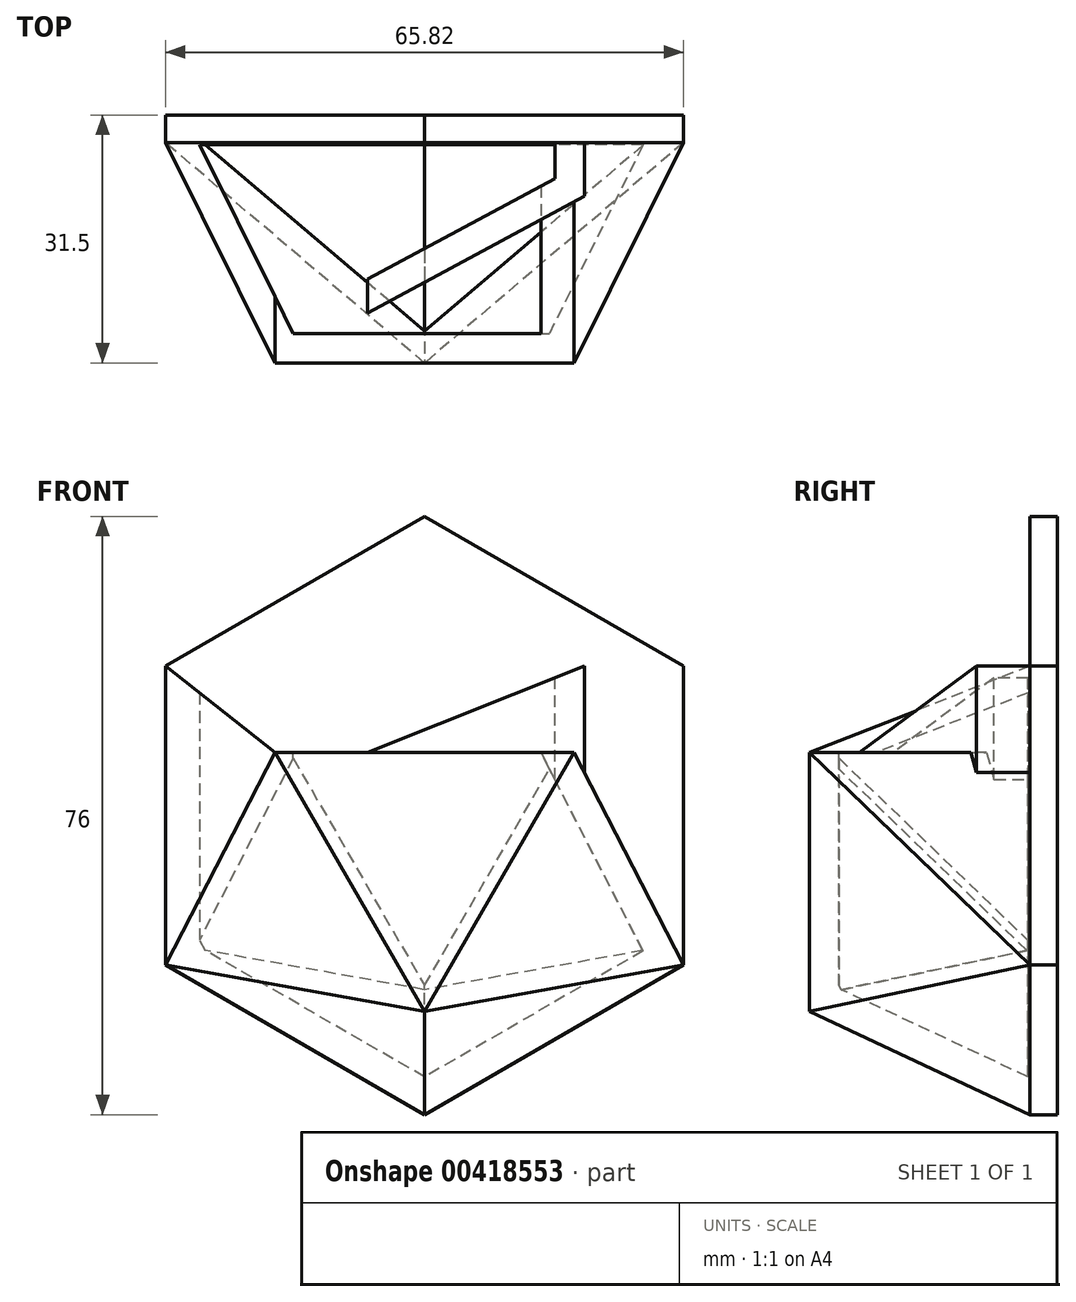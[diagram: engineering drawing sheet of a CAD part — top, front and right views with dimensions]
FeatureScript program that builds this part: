
annotation { "Feature Type Name" : "Feature", "Feature Type Description" : "" }
export const myFeature = defineFeature(function(context is Context, id is Id, definition is map)
    precondition{}
    {
        {
            var Q0;
            Q0=qCreatedBy(makeId("Front.planeOp"),FACE);
            var sketch = newSketch(context, id + "F0", { "sketchPlane" : qUnion([Q0])});
            skCircle(sketch, "E0.cCircle", {"center": v(0, 0) * mm, "radius": 38 * mm, "construction": true});
            skLineSegment(sketch, "E0.0", {"start": v(-32.9, 19) * mm, "end": v(0, 38) * mm});
            skLineSegment(sketch, "E0.1", {"start": v(0, 38) * mm, "end": v(32.9, 19) * mm});
            skLineSegment(sketch, "E0.2", {"start": v(32.9, 19) * mm, "end": v(32.9, -19) * mm});
            skLineSegment(sketch, "E0.3", {"start": v(32.9, -19) * mm, "end": v(0, -38) * mm});
            skLineSegment(sketch, "E0.4", {"start": v(0, -38) * mm, "end": v(-32.9, -19) * mm});
            skLineSegment(sketch, "E0.5", {"start": v(-32.9, -19) * mm, "end": v(-32.9, 19) * mm});
            skSolve(sketch);
        }
        {
            var Q0;
            Q0=qCreatedBy(makeId("Front.planeOp"),FACE);
            cPlane(context, id + "F1", {"entities" : qUnion([Q0]), "cplaneType" : CPlaneType.OFFSET, "offset" : 28 * mm, "width" : 150 * mm, "height" : 150 * mm});
        }
        {
            var Q0;
            Q0=qCreatedBy(id+"F1.planeOp",FACE);
            var sketch = newSketch(context, id + "F2", { "sketchPlane" : qUnion([Q0])});
            skLineSegment(sketch, "E1", {"start": v(-19, 8) * mm, "end": v(0, -24.9) * mm});
            skLineSegment(sketch, "E2", {"start": v(0, -24.9) * mm, "end": v(19, 8) * mm});
            skLineSegment(sketch, "E3", {"start": v(19, 8) * mm, "end": v(-19, 8) * mm});
            skSolve(sketch);
        }
        {
            var Q0;
            Q0=sQuery(id+"F2.wireOp",VERTEX,"E3.end");
            var Q1;
            Q1=sQuery(id+"F2.wireOp",VERTEX,"E2.start");
            var Q2;
            Q2=sQuery(id+"F0.wireOp",VERTEX,"E0.5.start");
            cPlane(context, id + "F3", {"entities" : qUnion([Q0, Q1, Q2]), "cplaneType" : CPlaneType.THREE_POINT, "offset" : 25 * mm, "width" : 150 * mm, "height" : 150 * mm});
        }
        {
            var Q0;
            Q0=qCreatedBy(id+"F3.planeOp",FACE);
            var sketch = newSketch(context, id + "F4", { "sketchPlane" : qUnion([Q0])});
            skLineSegment(sketch, "E4", {"start": v(23.37, -8.39) * mm, "end": v(-19.45, -16.66) * mm});
            skLineSegment(sketch, "E5", {"start": v(-19.45, -16.66) * mm, "end": v(-1.35, 20.47) * mm});
            skLineSegment(sketch, "E6", {"start": v(-1.35, 20.47) * mm, "end": v(23.37, -8.39) * mm});
            skSolve(sketch);
        }
        {
            var Q0;
            Q0=sQuery(id+"F0.wireOp",VERTEX,"E0.5.start");
            var Q1;
            Q1=sQuery(id+"F0.wireOp",VERTEX,"E0.5.end");
            var Q2;
            Q2=sQuery(id+"F2.wireOp",VERTEX,"E3.end");
            cPlane(context, id + "F5", {"entities" : qUnion([Q0, Q1, Q2]), "cplaneType" : CPlaneType.THREE_POINT, "offset" : 25 * mm, "width" : 150 * mm, "height" : 150 * mm});
        }
        {
            var Q0;
            Q0=qCreatedBy(id+"F5.planeOp",FACE);
            var sketch = newSketch(context, id + "F6", { "sketchPlane" : qUnion([Q0])});
            skLineSegment(sketch, "E7", {"start": v(16.62, 8) * mm, "end": v(-14.64, -19) * mm});
            skLineSegment(sketch, "E8", {"start": v(-14.64, -19) * mm, "end": v(-14.64, 19) * mm});
            skLineSegment(sketch, "E9", {"start": v(-14.64, 19) * mm, "end": v(16.62, 8) * mm});
            skSolve(sketch);
        }
        {
            var Q0;
            Q0=sQuery(id+"F2.wireOp",VERTEX,"E2.start");
            var Q1;
            Q1=sQuery(id+"F6.wireOp",VERTEX,"E8.start");
            var Q2;
            Q2=sQuery(id+"F0.wireOp",VERTEX,"E0.4.start");
            cPlane(context, id + "F7", {"entities" : qUnion([Q0, Q1, Q2]), "cplaneType" : CPlaneType.THREE_POINT, "offset" : 25 * mm, "width" : 150 * mm, "height" : 150 * mm});
        }
        {
            var Q0;
            Q0=qCreatedBy(id+"F7.planeOp",FACE);
            var sketch = newSketch(context, id + "F8", { "sketchPlane" : qUnion([Q0])});
            skLineSegment(sketch, "E10", {"start": v(15.95, -14.81) * mm, "end": v(-21.18, 8.05) * mm});
            skLineSegment(sketch, "E11", {"start": v(-21.18, 8.05) * mm, "end": v(15.95, 16.1) * mm});
            skLineSegment(sketch, "E12", {"start": v(15.95, 16.1) * mm, "end": v(15.95, -14.81) * mm});
            skSolve(sketch);
        }
        {
            var Q0;
            Q0=sQuery(id+"F8.wireOp",VERTEX,"E12.end");
            var Q1;
            Q1=sQuery(id+"F8.wireOp",VERTEX,"E12.start");
            var Q2;
            Q2=sQuery(id+"F0.wireOp",VERTEX,"E0.3.start");
            cPlane(context, id + "F9", {"entities" : qUnion([Q0, Q1, Q2]), "cplaneType" : CPlaneType.THREE_POINT, "offset" : 25 * mm, "width" : 150 * mm, "height" : 150 * mm});
        }
        {
            var Q0;
            Q0=qCreatedBy(id+"F9.planeOp",FACE);
            var sketch = newSketch(context, id + "F10", { "sketchPlane" : qUnion([Q0])});
            skLineSegment(sketch, "E13", {"start": v(-15.95, -14.81) * mm, "end": v(-15.95, 16.1) * mm});
            skLineSegment(sketch, "E14", {"start": v(-15.95, 16.1) * mm, "end": v(21.18, 8.05) * mm});
            skLineSegment(sketch, "E15", {"start": v(21.18, 8.05) * mm, "end": v(-15.95, -14.81) * mm});
            skSolve(sketch);
        }
        {
            var Q0;
            Q0=sQuery(id+"F10.wireOp",VERTEX,"E13.start");
            var Q1;
            Q1=sQuery(id+"F2.wireOp",VERTEX,"E3.start");
            var Q2;
            Q2=sQuery(id+"F10.wireOp",VERTEX,"E15.start");
            cPlane(context, id + "F11", {"entities" : qUnion([Q0, Q1, Q2]), "cplaneType" : CPlaneType.THREE_POINT, "offset" : 25 * mm, "width" : 150 * mm, "height" : 150 * mm});
        }
        {
            var Q0;
            Q0=qCreatedBy(id+"F11.planeOp",FACE);
            var sketch = newSketch(context, id + "F12", { "sketchPlane" : qUnion([Q0])});
            skLineSegment(sketch, "E16", {"start": v(-23.37, -8.39) * mm, "end": v(19.45, -16.66) * mm});
            skLineSegment(sketch, "E17", {"start": v(19.45, -16.66) * mm, "end": v(1.35, 20.47) * mm});
            skLineSegment(sketch, "E18", {"start": v(1.35, 20.47) * mm, "end": v(-23.37, -8.39) * mm});
            skSolve(sketch);
        }
        {
            var Q0;
            Q0=sQuery(id+"F0.wireOp",VERTEX,"E0.1.start");
            var Q1;
            Q1=sQuery(id+"F6.wireOp",VERTEX,"E9.end");
            var Q2;
            Q2=sQuery(id+"F6.wireOp",VERTEX,"E9.start");
            cPlane(context, id + "F13", {"entities" : qUnion([Q0, Q1, Q2]), "cplaneType" : CPlaneType.THREE_POINT, "offset" : 25 * mm, "width" : 150 * mm, "height" : 150 * mm});
        }
        {
            var Q0;
            Q0=qCreatedBy(id+"F13.planeOp",FACE);
            var sketch = newSketch(context, id + "F14", { "sketchPlane" : qUnion([Q0])});
            skLineSegment(sketch, "E19", {"start": v(-7.51, -18.66) * mm, "end": v(13.54, 21.36) * mm});
            skLineSegment(sketch, "E20", {"start": v(13.54, 21.36) * mm, "end": v(-22.93, 10.68) * mm});
            skLineSegment(sketch, "E21", {"start": v(-22.93, 10.68) * mm, "end": v(-7.51, -18.66) * mm});
            skSolve(sketch);
        }
        {
            var Q0;
            Q0=sQuery(id+"F12.wireOp",VERTEX,"E17.end");
            var Q1;
            Q1=sQuery(id+"F14.wireOp",VERTEX,"E20.start");
            var Q2;
            Q2=sQuery(id+"F14.wireOp",VERTEX,"E21.end");
            cPlane(context, id + "F15", {"entities" : qUnion([Q0, Q1, Q2]), "cplaneType" : CPlaneType.THREE_POINT, "offset" : 25 * mm, "width" : 150 * mm, "height" : 150 * mm});
        }
        {
            var Q0;
            Q0=qCreatedBy(id+"F15.planeOp",FACE);
            var sketch = newSketch(context, id + "F16", { "sketchPlane" : qUnion([Q0])});
            skLineSegment(sketch, "E22", {"start": v(19, -13.26) * mm, "end": v(0, 27.78) * mm});
            skLineSegment(sketch, "E23", {"start": v(0, 27.78) * mm, "end": v(-19, -13.26) * mm});
            skLineSegment(sketch, "E24", {"start": v(19, -13.26) * mm, "end": v(-19, -13.26) * mm});
            skSolve(sketch);
        }
        {
            var Q0;
            Q0=sQuery(id+"F0.wireOp",VERTEX,"E0.2.start");
            var Q1;
            Q1=sQuery(id+"F12.wireOp",VERTEX,"E17.start");
            var Q2;
            Q2=sQuery(id+"F16.wireOp",VERTEX,"E24.start");
            cPlane(context, id + "F17", {"entities" : qUnion([Q0, Q1, Q2]), "cplaneType" : CPlaneType.THREE_POINT, "offset" : 25 * mm, "width" : 150 * mm, "height" : 150 * mm});
        }
        {
            var Q0;
            Q0=qCreatedBy(id+"F17.planeOp",FACE);
            var sketch = newSketch(context, id + "F18", { "sketchPlane" : qUnion([Q0])});
            skLineSegment(sketch, "E25", {"start": v(-16.62, 8) * mm, "end": v(14.64, -19) * mm});
            skLineSegment(sketch, "E26", {"start": v(14.64, -19) * mm, "end": v(14.64, 19) * mm});
            skLineSegment(sketch, "E27", {"start": v(14.64, 19) * mm, "end": v(-16.62, 8) * mm});
            skSolve(sketch);
        }
        {
            var Q0;
            Q0=sQuery(id+"F18.wireOp",VERTEX,"E25.start");
            var Q1;
            Q1=sQuery(id+"F18.wireOp",VERTEX,"E27.start");
            var Q2;
            Q2=sQuery(id+"F16.wireOp",VERTEX,"E23.start");
            cPlane(context, id + "F19", {"entities" : qUnion([Q0, Q1, Q2]), "cplaneType" : CPlaneType.THREE_POINT, "offset" : 25 * mm, "width" : 150 * mm, "height" : 150 * mm});
        }
        {
            var Q0;
            Q0=qSketchRegion(id+"F0",true);
            extrude(context, id + "F20", {"entities" : qUnion([Q0]), "oppositeDirection" : true, "depth" : 3.5 * mm});
        }
        {
            var Q0;
            Q0=makeQuery(id+"F2.imprint","IMPRINT",FACE,{"disambiguationData":[TD([[makeQuery(id+"F2.imprint","IMPRINT",EDGE,{"derivedFrom":sQuery(id+"F2.wireOp",EDGE,"E1")}),1.0]])]});
            var Q1;
            Q1=makeQuery(id+"F6.imprint","IMPRINT",FACE,{"disambiguationData":[TD([[makeQuery(id+"F6.imprint","IMPRINT",EDGE,{"derivedFrom":sQuery(id+"F6.wireOp",EDGE,"E7")}),-1.0]])]});
            var Q2;
            Q2=makeQuery(id+"F4.imprint","IMPRINT",FACE,{"disambiguationData":[TD([[makeQuery(id+"F4.imprint","IMPRINT",EDGE,{"derivedFrom":sQuery(id+"F4.wireOp",EDGE,"E4")}),-1.0]])]});
            var Q3;
            Q3=makeQuery(id+"F8.imprint","IMPRINT",FACE,{"disambiguationData":[TD([[makeQuery(id+"F8.imprint","IMPRINT",EDGE,{"derivedFrom":sQuery(id+"F8.wireOp",EDGE,"E10")}),-1.0]])]});
            var Q4;
            Q4=makeQuery(id+"F10.imprint","IMPRINT",FACE,{"disambiguationData":[TD([[makeQuery(id+"F10.imprint","IMPRINT",EDGE,{"derivedFrom":sQuery(id+"F10.wireOp",EDGE,"E13")}),-1.0]])]});
            var Q5;
            Q5=makeQuery(id+"F12.imprint","IMPRINT",FACE,{"disambiguationData":[TD([[makeQuery(id+"F12.imprint","IMPRINT",EDGE,{"derivedFrom":sQuery(id+"F12.wireOp",EDGE,"E16")}),1.0]])]});
            var Q6;
            Q6=makeQuery(id+"F18.imprint","IMPRINT",FACE,{"disambiguationData":[TD([[makeQuery(id+"F18.imprint","IMPRINT",EDGE,{"derivedFrom":sQuery(id+"F18.wireOp",EDGE,"E25")}),1.0]])]});
            var Q7;
            Q7=makeQuery(id+"F20.opExtrude","CAP_FACE",FACE,{"disambiguationData":[OSD([sQuery(id+"F0.wireOp",EDGE,"E0.0"),sQuery(id+"F0.wireOp",EDGE,"E0.1"),sQuery(id+"F0.wireOp",EDGE,"E0.2"),sQuery(id+"F0.wireOp",EDGE,"E0.3"),sQuery(id+"F0.wireOp",EDGE,"E0.4"),sQuery(id+"F0.wireOp",EDGE,"E0.5")])],"isStart":true});
            extrude(context, id + "F21", {"entities" : qUnion([Q0, Q1, Q2, Q3, Q4, Q5, Q6]), "operationType" : NewBodyOperationType.ADD, "endBound" : BoundingType.UP_TO_SURFACE, "oppositeDirection" : true, "endBoundEntityFace" : qUnion([Q7]), "depth" : 25 * mm});
        }
        {
            var Q0;
            Q0=makeQuery(id+"F21.opExtrude","SWEPT_FACE",FACE,{"disambiguationData":[OSD([sQuery(id+"F2.wireOp",EDGE,"E3")])]});
            var Q1;
            Q1=makeQuery(id+"F21.opExtrude","SWEPT_FACE",FACE,{"disambiguationData":[OSD([sQuery(id+"F18.wireOp",EDGE,"E27")])]});
            var Q2;
            Q2=makeQuery(id+"F21.opExtrude","SWEPT_FACE",FACE,{"disambiguationData":[OSD([sQuery(id+"F6.wireOp",EDGE,"E9")])]});
            var Q3;
            Q3=makeQuery(id+"F21.opExtrude","SWEPT_FACE",FACE,{"disambiguationData":[OSD([sQuery(id+"F2.wireOp",EDGE,"WbOHPHKK-Nw33-ZnTN-OlqM-fbYxj0YIFz8h")])]});
            var Q4;
            Q4=makeQuery(id+"F21.opExtrude","SWEPT_FACE",FACE,{"disambiguationData":[OSD([sQuery(id+"F2.wireOp",EDGE,"5qjFDsdd-swa0-z9kg-JQke-vFuo6n7Ob3zi")])]});
            var Q5;
            Q5=makeQuery(id+"F21.opExtrude","SWEPT_FACE",FACE,{"disambiguationData":[OSD([sQuery(id+"F2.wireOp",EDGE,"GYQIImPS-komu-qjez-Sc8f-C5i2az53FD9t")])]});
            shell(context, id + "F22", {"entities" : qUnion([Q0, Q1, Q2, Q3, Q4, Q5]), "thickness" : 3.75 * mm});
        }
    });
